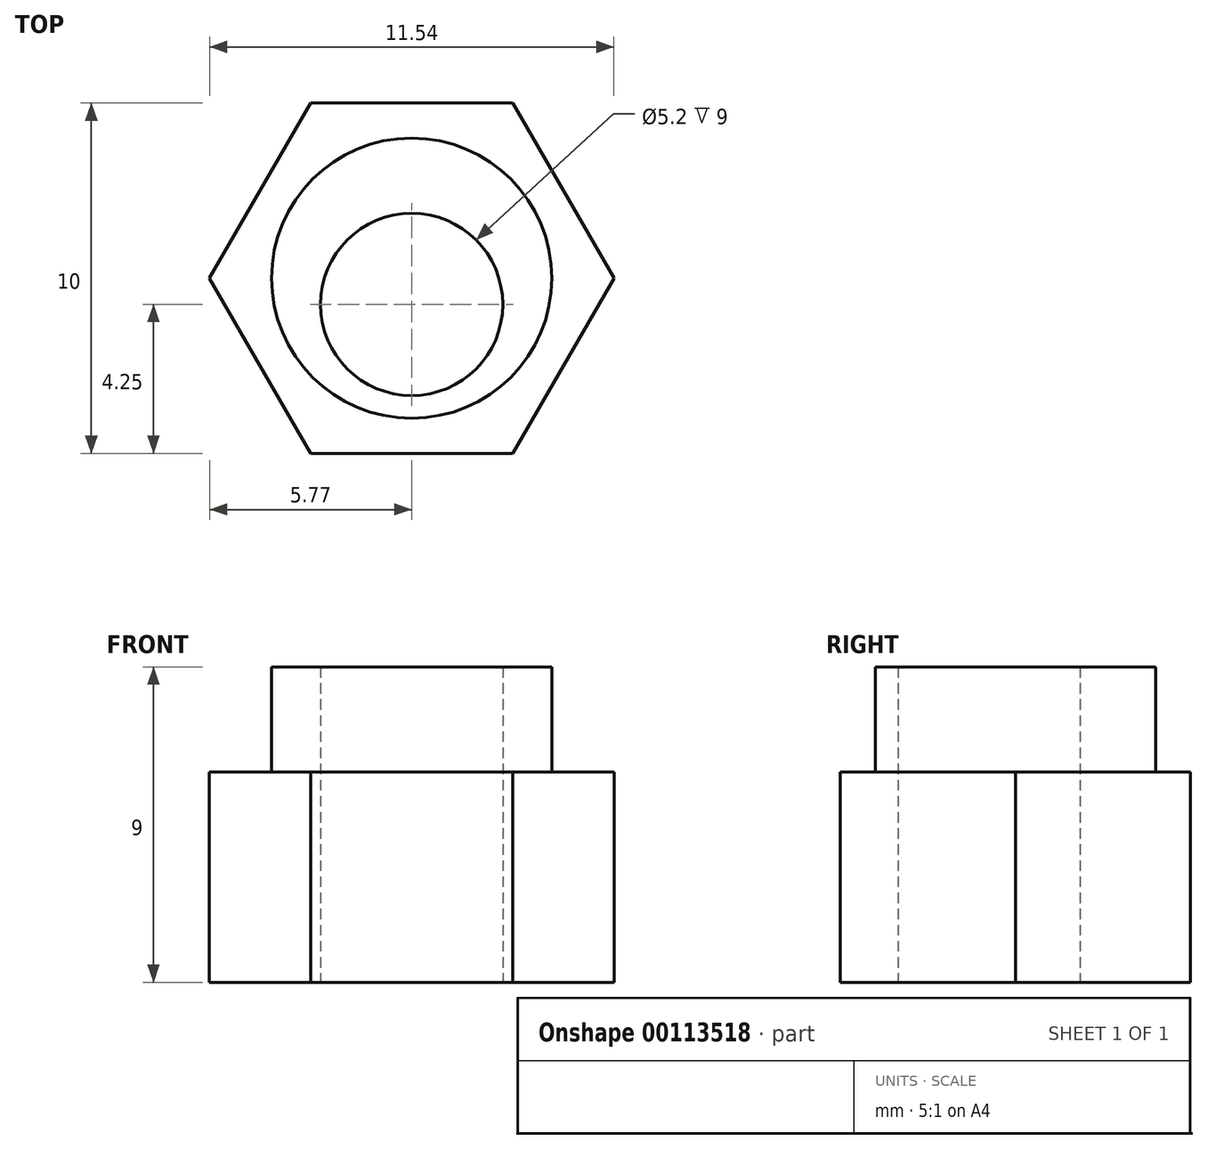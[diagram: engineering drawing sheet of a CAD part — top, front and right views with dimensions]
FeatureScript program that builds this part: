
annotation { "Feature Type Name" : "Feature", "Feature Type Description" : "" }
export const myFeature = defineFeature(function(context is Context, id is Id, definition is map)
    precondition{}
    {
        {
            assignVariable(context, id + "F0", {"name" : "SpacerDistance", "anyValue" : 6 * mm});
        }
        {
            assignVariable(context, id + "F1", {"name" : "PortletDistance", "anyValue" : 3 * mm});
        }
        {
            var Q0;
            Q0=qCreatedBy(makeId("Top.planeOp"),FACE);
            var sketch = newSketch(context, id + "F2", { "sketchPlane" : qUnion([Q0])});
            skCircle(sketch, "E0.cCircle", {"center": v(0, 0) * mm, "radius": 5 * mm, "construction": true});
            skLineSegment(sketch, "E0.0", {"start": v(-2.89, 5) * mm, "end": v(2.89, 5) * mm});
            skLineSegment(sketch, "E0.1", {"start": v(2.89, 5) * mm, "end": v(5.77, 0) * mm});
            skLineSegment(sketch, "E0.2", {"start": v(5.77, 0) * mm, "end": v(2.89, -5) * mm});
            skLineSegment(sketch, "E0.3", {"start": v(2.89, -5) * mm, "end": v(-2.89, -5) * mm});
            skLineSegment(sketch, "E0.4", {"start": v(-2.89, -5) * mm, "end": v(-5.77, 0) * mm});
            skLineSegment(sketch, "E0.5", {"start": v(-5.77, 0) * mm, "end": v(-2.89, 5) * mm});
            skPoint(sketch, "E0.0.midPoint", {"position": v(0, 5) * mm});
            skCircle(sketch, "E1", {"center": v(0, -0.75) * mm, "radius": 2.6 * mm});
            skCircle(sketch, "E2", {"center": v(0, 0) * mm, "radius": 4 * mm});
            skSolve(sketch);
        }
        {
            var Q0;
            Q0=makeQuery(id+"F2.imprint","IMPRINT",FACE,{"disambiguationData":[TD([[makeQuery(id+"F2.imprint","IMPRINT",EDGE,{"derivedFrom":sQuery(id+"F2.wireOp",EDGE,"E0.0")}),-1.0]])]});
            var Q1;
            Q1=makeQuery(id+"F2.imprint","IMPRINT",FACE,{"disambiguationData":[TD([[makeQuery(id+"F2.imprint","IMPRINT",EDGE,{"derivedFrom":sQuery(id+"F2.wireOp",EDGE,"E1")}),-1.0]])]});
            extrude(context, id + "F3", {"entities" : qUnion([Q0, Q1]), "depth" : getVariable(context, 'SpacerDistance')});
        }
        {
            var Q0;
            Q0=makeQuery(id+"F2.imprint","IMPRINT",FACE,{"disambiguationData":[TD([[makeQuery(id+"F2.imprint","IMPRINT",EDGE,{"derivedFrom":sQuery(id+"F2.wireOp",EDGE,"E1")}),-1.0]])]});
            extrude(context, id + "F4", {"entities" : qUnion([Q0]), "operationType" : NewBodyOperationType.ADD, "depth" : getVariable(context, 'SpacerDistance') + getVariable(context, 'PortletDistance')});
        }
    });
